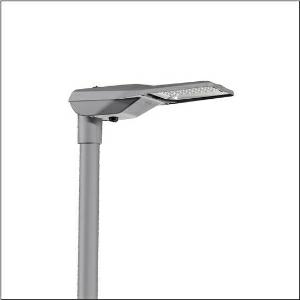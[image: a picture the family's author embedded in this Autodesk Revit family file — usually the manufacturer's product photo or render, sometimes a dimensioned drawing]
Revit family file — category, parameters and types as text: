
# Revit family: streetlight_sl_21_iq_mini___pl52_5xe2h31y08hb_fa04
name_source: partatom
category: Lighting Fixtures
units: mm (PartAtom-declared; Revit-internal decimal feet)

## family parameters
Cut with Voids When Loaded = No
Host = Face
Light Source = No
Part Type = Normal
Room Calculation Point = No
Round Connector Dimension = Use Diameter
Shared = No

## types (1)
- --- (1 x LED, 9580 lm, 71 W, 3000K)
    Apparent Load = 71 VA
    CIE Flux Codes = 27 59 98 100 100
    Color Rendering = 70
    Color Temperature = 3000K
    Default Elevation = 1800 mm
    Description = Streetlight SL 21 iQ mini, mast luminaire, primary light control with lens, of PMMA, primary optical cover: cover, of toughened safety glass, transparent, light distribution: PL52, light emission: direct distribution, primary light characteristic: asymmetric, installation type: post-top, side-entry, LED, High Power LED, rated luminous flux: 9.580lm, luminous efficacy: 135lm/W, light colour: 730, colour temperature: 3000K, control gear: iQ-Street Remote, D4i with power reduction, control: pre-setting: logarithmic dimming characteristic, Street-Remote, Auto-Match, Temp-Guard, Lumen-Switch, Night-Set, Smart-Wire, Light-Fading, Desk-Remote (wireless, voltage-free reading and setting of iQ features in the workshop via application-optimized NFC function/RFID function), optimised constant luminous flux control (CLO 2.0), mains connection: 220..240V, AC, 50/60Hz, start of lifetime: 71W, end of service life: 75W, reduction: 30W, luminaire housing, of diecast aluminium, powder-coated, Siteco® metallic grey (DB 702S), corrosivity category C5 mid according to DIN EN ISO 12944, please order mast flange separately, inclination adjustable: 0°, 5°, 10°, 15°, sealing non-destructively replaceable, multi-level sealing system, length: 628mm, width: 235mm, height: 110mm, mast flange for spigot size: 42mm (side-entry): 5XC10008XM4, 60/48mm (side-entry/post-top): 5XC10108XM2, 76/60mm (side-entry/post-top): 5XC10108XM1, mounting height: 4..8m, Smart Interface below and above, protection rating (complete): IP66, insulation class (complete): insulation class II (safety insulation), certification: CE, ENEC, ENEC+, VDE, impact resistance: IK10, permissible operating ambient temperature for outdoor applications: -40..+50°C, standard-compliant lighting for roads and squares, packaging unit: 1 piece

Light Distribution: PL52
    Height = 110 mm
    Lamp = 1 x LED
    Lamp Light Flux = 9580 lm
    Lamp Power = 71 W
    Lamp count = 1
    Length = 625 mm
    Luminous efficacy = 135 lm/W
    Manufacturer = Siteco
    ModVariant = No
    Model = 5XE2H31Y08HB
    Number of Poles = 1
    OnlyDefault = Yes
    Power Factor = 1
    Product Name = Streetlight SL 21 iQ mini | PL52
    Product group = mast luminaire | pylon top
    ProductGroupID = 6100
    Protection Class = Protection class II
    Protection Degree = IP 66
    RLX_Detail_Level = 1
    RLX_Emergency_Light_Flux = 0 lm
    RLX_Emergency_Type = 0
    RLX_Emergency_Type_DB = No
    RlxData = <blob elided: 36305 chars, md5=8c5278ba>
    Socket = socket
    Standby Power = 0 W
    System Light Flux = 9580 lm
    System Power = 71 W
    Type Comments = factory setting: luminous flux: 100 % | dim-lin: 254 | 716 mA
    Type Image = l_1003514.jpg
    URL = http://relux.com
    VarID = @adj_115912
    Voltage = 0 V
    Weight = 0.00 kg
    Width = 234 mm

## geometry (parser evidence)
native form markers: Blend x4, Sweep x11
no freeform markers — native parametric forms only
